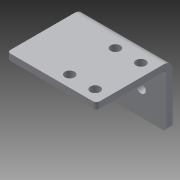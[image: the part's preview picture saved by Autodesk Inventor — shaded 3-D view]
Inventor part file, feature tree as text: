
AUTODESK INVENTOR PART (.ipt)
format: ipt  version: 2014 (Build 180170000, 170)  size: 198,144 bytes
history: native  units: in
note: dims shown in document units (in); Inventor stores cm internally (conversion verified against a paired STEP export)
features: sheet_metal_op x4, other x4, sketch x3, fillet x1, extrude x1
ambient origin geometry x8: Origin, YZ Plane, XZ Plane, XY Plane, X Axis, Y Axis, Z Axis, Center Point
bodies: Solid1 (feature_tree)
feature tree (13):
  sheet_metal_op  "Face1"
  sheet_metal_op  "Flange1"
  fillet  "Fillet1"  Radius=1.75in
  extrude  "Extrusion1"  Depth=0.19in
  sketch  "Sketch1"  dims[d1=1.0in d2=0.19in]
  other  "Plate1"
  sketch  "Sketch2"  dims[d4=0.7874in d6=1.0in d7=0.3937in d9=1.0in]
  other  "Plate2"
  sheet_metal_op  "Bend1"
  sheet_metal_op  "Corner1"
  sketch  "Sketch3"  dims[d11=0.125in d12=0.125in d13=0.0625in d14=0.25in d15=0.125in d16=1.5in d17=90.0deg d18=0.05in d19=0.5in d20=0.125in d21=0.125in d22=0.0625in d23=1.35in d24=0.75in d27=0.19in d28=0.125in d29=0.2265in d30=1.0in d31=0.0in d34=0.25in d35=0.875in d3=0.0in d5=0.1649in d8=0.025in d10=0.025in]
  other  "Definition1"
  other  "Cut1"
